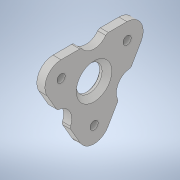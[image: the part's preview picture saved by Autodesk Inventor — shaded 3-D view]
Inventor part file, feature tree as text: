
AUTODESK INVENTOR PART (.ipt)
format: ipt  version: 2021 (Build 250183000, 183)  size: 193,536 bytes
history: native  units: in
note: dims shown in document units (in); Inventor stores cm internally (conversion verified against a paired STEP export)
features: extrude x2, chamfer x2, sketch x2, fillet x1
ambient origin geometry x8: Origin, YZ Plane, XZ Plane, XY Plane, X Axis, Y Axis, Z Axis, Center Point
bodies: Solid1 (feature_tree)
feature tree (7):
  extrude  "Extrusion1"  Depth=0.125in TaperAngle=360.0deg
  fillet  "Fillet2"  Radius=0.125in
  extrude  "Extrusion3"  Depth=0.125in
  chamfer  "Chamfer5"  Distance=0.3153in
  chamfer  "Chamfer7"  Distance=1.25in
  sketch  "Sketch1"  dims[d4=0.3125in d5=0.0in d26=1.1811in d28=360.0deg d30=0.125in]
  sketch  "Sketch5"  dims[d34=1.25in d35=1.135in d36=0.3153in d37=1.25in d38=1.25in d39=60.0deg d40=60.0deg d41=0.2903in d42=2.1897in d43=2.1897in d44=0.0in d45=1.6222in d46=0.0in d47=2.4668in d48=3.1515in d49=0.0in d50=3.1515in d51=0.625in d52=0.625in d53=0.9375in d54=3.1515in d55=1.363in d56=1.363in d57=1.6222in d58=0.0in d59=1.6222in d60=2.4668in d61=2.4668in d62=0.0in d63=2.4668in d64=1.6222in d65=2.839in d66=3.1515in d67=0.0in d68=3.1515in d69=0.9375in d70=1.0in d71=1.0in d72=0.0in d76=0.1875in d77=0.125in d78=45.0deg d82=0.03in d83=0.125in d84=45.0deg]
